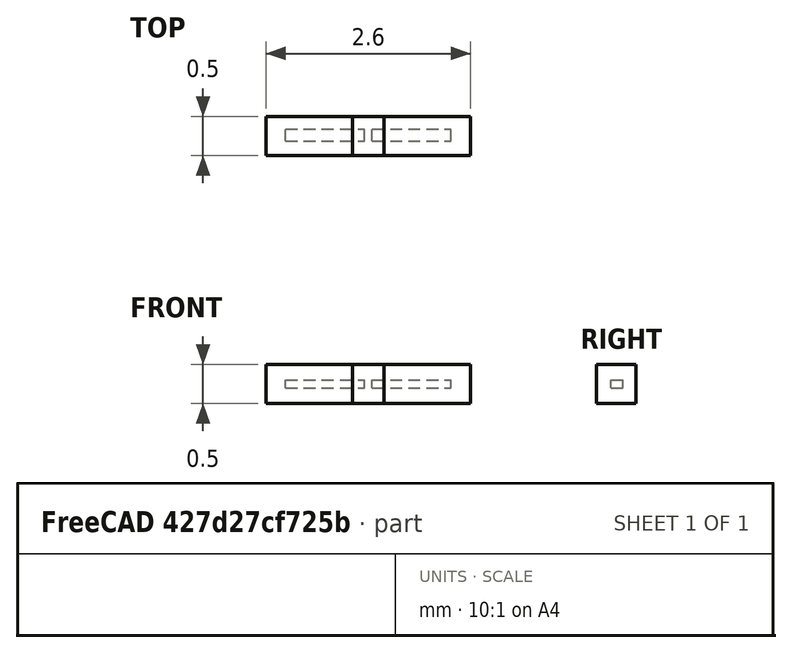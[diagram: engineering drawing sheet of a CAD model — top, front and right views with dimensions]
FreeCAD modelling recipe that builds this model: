
FCSTD DOCUMENT  (FreeCAD 1.0R39109 (Git))
Label: background
License: All rights reserved
LicenseURL: https://en.wikipedia.org/wiki/All_rights_reserved
objects: Part::Feature×6, Part::Box×4, Part::FeaturePython×2, App::DocumentObjectGroupPython×2
note: 12 computed .brp shape members not serialized (recipe doc carries the construction recipe); baked Part::Feature solids carry a one-line shape summary decoded from their .brp

FEATURE [Part::Box] Box  label="hullWall1"
  AttacherType = Attacher::AttachEngine3D
  Height = 0.1
  Length = 1
  Placement = pos=(0,-0.075,-0.05) rot=(0,0,1;0rad)
  Width = 0.15
FEATURE [Part::Box] Box001  label="hullWall2"
  AttacherType = Attacher::AttachEngine3D
  Height = 0.1
  Length = 1
  Placement = pos=(-1.1,-0.075,-0.05) rot=(0,0,1;0rad)
  Width = 0.15
FEATURE [Part::Feature] Face  label="outlet"
  Placement = pos=(-1.5,-0.5,-0.5) rot=(0,0,1;0rad)
  shape: bbox 2e-07 x 1 x 1 mm, 1 faces, 0 solids (baked)
FEATURE [Part::Feature] Face001  label="inlet"
  Placement = pos=(-1.5,-0.5,-0.5) rot=(0,0,1;0rad)
  shape: bbox 2e-07 x 1 x 1 mm, 1 faces, 0 solids (baked)
FEATURE [Part::Feature] Face002  label="front"
  Placement = pos=(-1.5,-0.5,-0.5) rot=(0,0,1;0rad)
  shape: bbox 5 x 2e-07 x 1 mm, 1 faces, 0 solids (baked)
FEATURE [Part::Feature] Face003  label="back"
  Placement = pos=(-1.5,-0.5,-0.5) rot=(0,0,1;0rad)
  shape: bbox 5 x 2e-07 x 1 mm, 1 faces, 0 solids (baked)
FEATURE [Part::Feature] Face004  label="base"
  Placement = pos=(-1.5,-0.5,-0.5) rot=(0,0,1;0rad)
  shape: bbox 5 x 1 x 2e-07 mm, 1 faces, 0 solids (baked)
FEATURE [Part::Feature] Face005  label="atomosphere"
  Placement = pos=(-1.5,-0.5,-0.5) rot=(0,0,1;0rad)
  shape: bbox 5 x 1 x 2e-07 mm, 1 faces, 0 solids (baked)
FEATURE [Part::Box] Box002  label="overset1"
  AttacherType = Attacher::AttachEngine3D
  Height = 0.5
  Length = 1.5
  Placement = pos=(-0.25,-0.26,-0.25) rot=(0,0,1;0rad)
  Width = 0.5
FEATURE [Part::Box] Box003  label="overset2"
  AttacherType = Attacher::AttachEngine3D
  Height = 0.5
  Length = 1.5
  Placement = pos=(-1.35,-0.26,-0.25) rot=(0,0,1;0rad)
  Width = 0.5
FEATURE [Part::FeaturePython] CfdSolver  # WARN: FeaturePython — macro-defined, semantics opaque (R4)
  Parallel = true
  ParallelCores = 1
  ParallelMethod = 0
FEATURE [Part::FeaturePython] MeshRefinement  # WARN: FeaturePython — macro-defined, semantics opaque (R4)
  AllowDiscont = true
  CellSize = 0.05
  ExpansionRatio = 1.2
  FirstLayerHeight = 0
  Internal = false
  KeepCell = false
  NumberLayers = 1
  RefinementLevel = 0
  RefinementThickness = 0
  RemoveCell = false
  ShapeRefs = -> [Face004,Face003,Face002]
  patchType = 2
FEATURE [App::DocumentObjectGroupPython] CFDMesh  # scripted group (container) (typed FeaturePython)
  BaseCellSize = 0.025
  ElementDimension = 1
  FeatureAngle = 30
  Group = -> [MeshRefinement]
  MeshUtility = 0
  ScaleToMeter = 1
  keepCellsIntersectingBoundary = false
  opt_featureSizeFactor = 0.4
  opt_maxNumIterations = 5
  opt_nSmoothNormals = 3
  opt_reCalculateNormals = true
  opt_relThicknessTol = 0.05
  optimiseLayer = false
  patchTypeSetting = false
  workflowControls = 0
FEATURE [App::DocumentObjectGroupPython] dexcsCfdAnalysis  # scripted group (container) (typed FeaturePython)
  Group = -> [CFDMesh,CfdSolver]
  IsActiveAnalysis = true
  NeedsCaseRewrite = true
  NeedsMeshRerun = true
  NeedsMeshRewrite = true
  PlotMaxnumber = 5000
  PlotMethodLast = false
